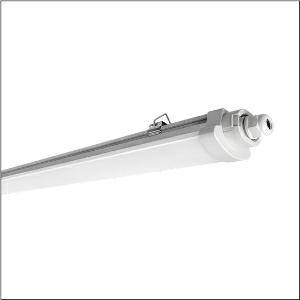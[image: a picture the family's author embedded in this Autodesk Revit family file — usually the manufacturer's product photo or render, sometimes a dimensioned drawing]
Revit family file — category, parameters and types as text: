
# Revit family: monsun_r__41_51fk20mk440a_a1bd
name_source: partatom
category: Lighting Fixtures
units: mm (PartAtom-declared; Revit-internal decimal feet)

## family parameters
Cut with Voids When Loaded = No
Host = Face
Light Source = No
Part Type = Normal
Room Calculation Point = No
Round Connector Dimension = Use Diameter
Shared = No

## types (1)
- --- (1 x LED, 4000 lm, 30 W, 4000K)
    Apparent Load = 30 VA
    CIE Flux Codes = 44 74 92 92 100
    Color Rendering = 80
    Color Temperature = 4000K
    Default Elevation = 1800 mm
    Description = Monsun® 41, damp-proof luminaire, primary optical cover: diffuser, of PC, frosted, light emission: direct distribution, primary light characteristic: symmetric, installation type: surface-mounted, suspended mounting, LED, rated luminous flux: 4.000lm, luminous efficacy: 130lm/W, light colour: 840, colour temperature: 4000K, control gear: ECG Multilumen, with terminal, 3-pole, mains connection: 220..240V, AC, 50/60Hz, rated input power: 30W, housing, luminaire housing, of PC, grey, length: 1.200mm, width: 79mm, height: 52mm, end cap, of PC, grey, ceiling mounting element, of stainless steel (V2A), protection rating (complete): IP65, insulation class (complete): insulation class II (safety insulation), certification: CE, UKCA, protection symbol: D, impact resistance: IK08, permissible operating ambient temperature: -20..+35°C, corresponds to IFS (International Featured Standards) requirements for safety and quality in the food industry, contact your sales advisor before using the luminaires in applications with unclear chemical exposure, large temperature fluctuations or condensation-forming humidity, packaging unit: 1 piece
    Height = 54 mm
    Lamp = 1 x LED
    Lamp Light Flux = 4000 lm
    Lamp Power = 30 W
    Lamp count = 1
    Length = 1200 mm
    Luminous efficacy = 133 lm/W
    Manufacturer = Siteco
    ModVariant = No
    Model = 51FK20MK440A
    Mounting Place = Ceiling
    Mounting Type = Surface mounted
    Number of Poles = 1
    OnlyDefault = Yes
    Power Factor = 1
    Product Name = Monsun® 41
    Product group = damp-proof luminaire
    ProductGroupID = 300
    Protection Class = Protection class II
    Protection Degree = IP 65
    RLX_Detail_Level = 1
    RLX_Emergency_Light_Flux = 0 lm
    RLX_Emergency_Type = 0
    RLX_Emergency_Type_DB = No
    RlxData = <blob elided: 31953 chars, md5=1c209c8c>
    Socket = socket
    Standby Power = 0 W
    System Light Flux = 4000 lm
    System Power = 30 W
    Type Comments = factory setting: luminous flux: 100 % | (HIGH)
    Type Image = l_1007037.jpg
    URL = http://relux.com
    VarID = @adj_107857
    Voltage = 0 V
    Weight = 0.00 kg
    Width = 79 mm

## geometry (parser evidence)
native form markers: Blend x4, Sweep x12
no freeform markers — native parametric forms only
